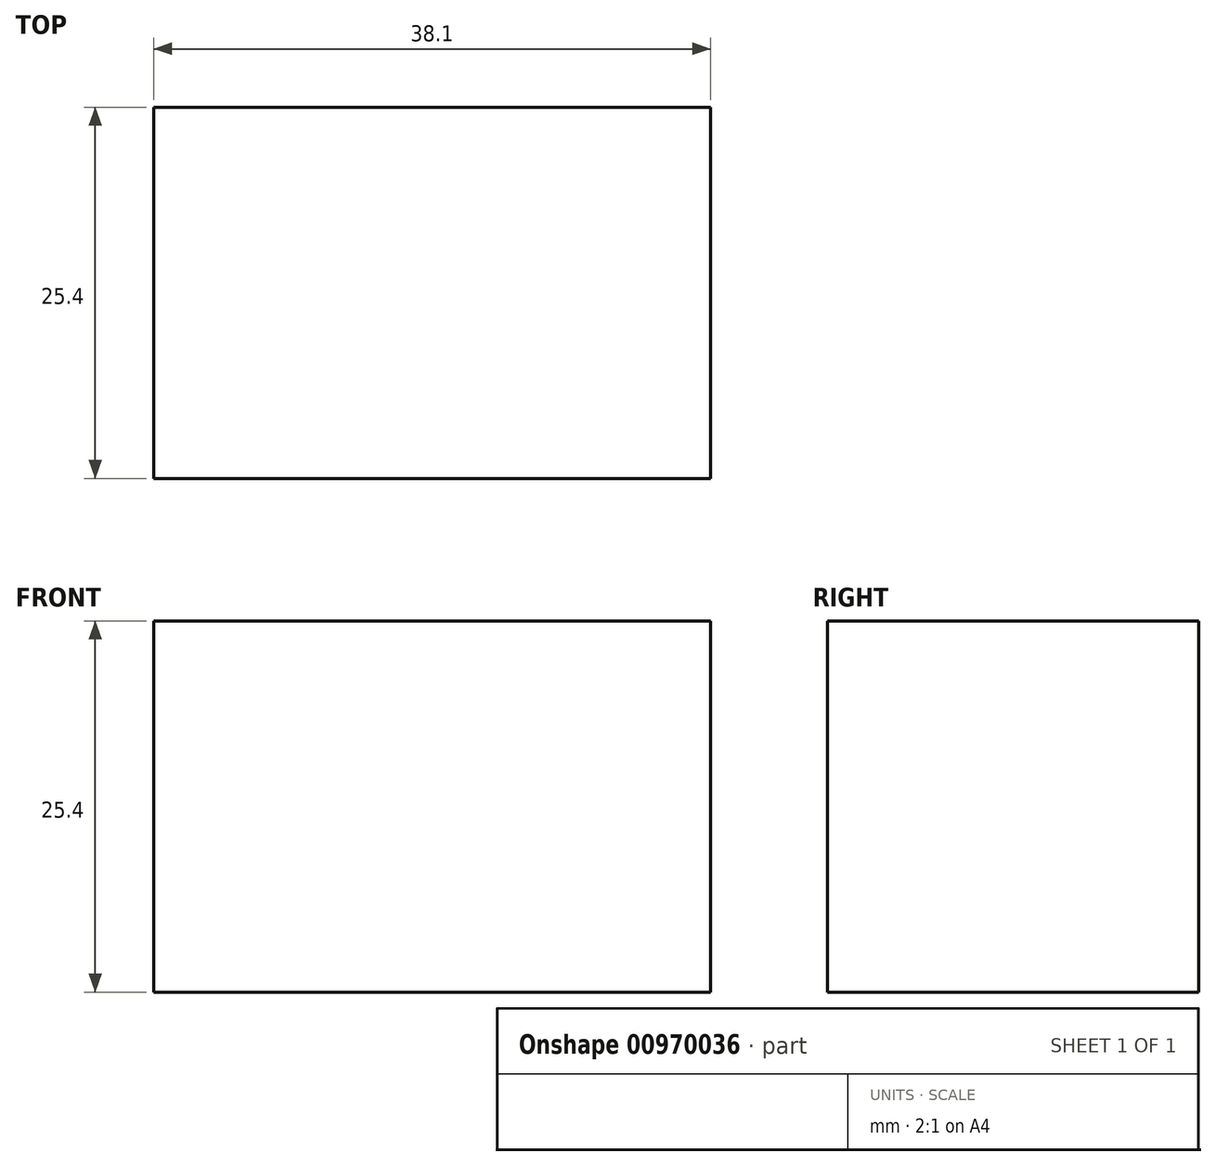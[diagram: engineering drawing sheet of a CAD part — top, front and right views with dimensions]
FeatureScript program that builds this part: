
annotation { "Feature Type Name" : "Feature", "Feature Type Description" : "" }
export const myFeature = defineFeature(function(context is Context, id is Id, definition is map)
    precondition{}
    {
        {
            var Q0;
            Q0=qCreatedBy(makeId("Front.planeOp"),FACE);
            var sketch = newSketch(context, id + "F0", { "sketchPlane" : qUnion([Q0])});
            skLineSegment(sketch, "E0.bottom", {"start": v(-38.1, 25.4) * mm, "end": v(0, 25.4) * mm});
            skLineSegment(sketch, "E0.top", {"start": v(-38.1, 0) * mm, "end": v(0, 0) * mm});
            skLineSegment(sketch, "E0.left", {"start": v(-38.1, 25.4) * mm, "end": v(-38.1, 0) * mm});
            skLineSegment(sketch, "E0.right", {"start": v(0, 25.4) * mm, "end": v(0, 0) * mm});
            skSolve(sketch);
        }
        {
            var Q0;
            Q0 = qSketchRegion(id + "F0", true);
            extrude(context, id + "F1", {"entities" : qUnion([Q0]), "depth" : 25.4 * mm, "offsetDistance" : 25.4 * mm});
        }
    });
